# Revit family: EXPLORER-R100
name_source: partatom
category: Осветительные приборы
revit_build: Autodesk Revit 2017 (Build: 20160225_1515(x64)
units: mm (PartAtom-declared; Revit-internal decimal feet)

## family parameters
Источник света = Нет
Общий = Нет
Основа = Грань
При загрузке вырезать с полостями = Нет
Размер круглого соединителя = Использовать диаметр
Тип детали = Нормальный
Точка расчета площади = Нет

## types (4) — shared parameters
ADSK_Единица измерения = шт.
ADSK_Завод-изготовитель = ARLIGHT
ADSK_Классификация нагрузок = Освещение
ADSK_Количество фаз = 1
ADSK_Количество фаз числовое = 1
ADSK_Коэффициент мощности = 0.85
ADSK_Масса_Текст = 0.397
ADSK_Наименование = Светильник
ADSK_Напряжение = 230 В
ADSK_Номинальная мощность = 12 Вт
ADSK_Полная мощность = 14 В·А
ADSK_Размер_Высота = 85 мм
ADSK_Размер_Диаметр = 99 мм
ADSK_Ток = 0 А
ARL_Драйвер = В комплекте (300mA 20-40V)
ARL_Индекс цветопередачи = >90
ARL_Класс защиты от поражения электрическим током = II
ARL_Класс пылевлагозащиты = IP20
ARL_Материал корпуса = Металл, белый
ARL_Область использования = Для освещения торговых, офисных, жилых и других помещений
ARL_Обозначение корпуса = Корпус круглый, металл, цвет белый
ARL_Рабочая температура окружающей среды = -10...+50 °C
ARL_Серия = EXPLORER
ARL_Способ монтажа = Встраиваемый
ARL_Тип товара = Светильник
ARL_Угол обзора = 38°
ARL_Цвет покрытия = Белый
URL = https://arlight.ru
Группа модели = Светильники
Изготовитель = ARLIGHT
Изготовитель (сайт) = www.arlight.ru
Изготовитель (телефон) = 8 800 505 26 29
Отметка по умолчанию = 1219 мм
Полная установленная мощность = 14 В·А
Разработчик = НТЦ Конструктор
Разработчик (URL) = https://constructor.ru
Разработчик (телефон) = +7 (495) 781-05-35

## per-type parameters (varying)
| type | ADSK_Код изделия | ADSK_Марка | ARL_Цвет свечения | Ies | Комментарии к типоразмеру | Описание |
| 024026 Светильник LTD-EXPLORER-R100-12W Warm3000 (WH, 38 deg) | Арт. 024026 | LTD-EXPLORER-R100-12W Warm3000 | Теплый 3000K | Семейство : 024026 ies | Арт. 024026 | Встраиваемый поворотный круглый светильник, угол 38° / 12 Вт / ТЕПЛЫЙ БЕЛЫЙ 3000K / 960-1080лм, CRI>90. Питание AC180-240V, драйвер в комплекте 300mA 20-40V). Размеры DxH: Ø99х85 мм, отверстие для установки 90 мм. Поворачивается вокруг своей оси на 350° и выдвигается на 45° |
| 024027 Светильник LTD-EXPLORER-R100-12W Day4000 (WH, 38 deg) | Арт. 024027 | LTD-EXPLORER-R100-12W Day4000 | Дневной 4000K | Семейство : 024027 ies | Арт. 024027 | Встраиваемый поворотный круглый светильник, угол 38° / 12 Вт / ДНЕВНОЙ БЕЛЫЙ 4000K / 960-1080лм, CRI>90. Питание AC180-240V, драйвер в комплекте 300mA 20-40V). Размеры DxH: Ø99х85 мм, отверстие для установки 90 мм. Поворачивается вокруг своей оси на 350° и выдвигается на 45° |
| 024028 Светильник LTD-EXPLORER-R100-12W White6000 (WH, 38 deg) | Арт. 024028 | LTD-EXPLORER-R100-12W White6000 | Белый 6000K | Семейство : 024028 ies | Арт. 024028 | Встраиваемый поворотный круглый светильник, угол 38° / 12 Вт / БЕЛЫЙ 6000K / 960-1080лм, CRI>90. Питание AC180-240V, драйвер в комплекте 300mA 20-40V). Размеры DxH: Ø99х85 мм, отверстие для установки 90 мм. Поворачивается вокруг своей оси на 350° и выдвигается на 45° |
| 026836 Светильник LTD-EXPLORER-R100-12W Day5000 (WH, 38 deg) | Арт. 026836 | LTD-EXPLORER-R100-12W Day5000 | Белый 5000K | Семейство : 026836 ies | Арт. 026836 | Встраиваемый поворотный круглый светильник, угол 38° / 12 Вт / ДНЕВНОЙ БЕЛЫЙ 5000K / 960-1080лм, CRI>90. Питание AC180-240V, драйвер в комплекте 300mA 20-40V). Размеры DxH: Ø99х85 мм, отверстие для установки 90 мм. Поворачивается вокруг своей оси на 350° и выдвигается на 45° |
